AUTODESK INVENTOR PART (.ipt)
format: ipt  version: 2023 (Build 270158000, 158)  size: 252,416 bytes
history: native  units: mm
features: sketch x1
ambient origin geometry x8: Origin, YZ Plane, XZ Plane, XY Plane, X Axis, Y Axis, Z Axis, Center Point
feature tree (1):
  sketch  "Sketch2"  dims[d29=59.42mm d30=13.56mm d31=8.85mm d32=8.06mm d33=9.16mm d35=10.67mm d36=8.56mm d37=8.03mm d38=6.54mm d39=10.41mm d40=7.01mm d41=11.97mm d42=11.35mm d43=6.73mm d44=12.88mm d45=4.91mm d46=12.83mm d47=11.47mm d48=12.63mm d49=6.69mm d50=3.2mm d51=1.6mm d52=14.53mm d53=3.6mm]
